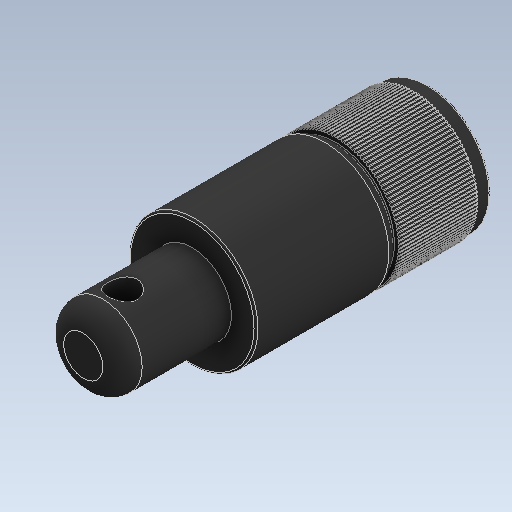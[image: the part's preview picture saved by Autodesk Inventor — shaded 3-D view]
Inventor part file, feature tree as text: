
AUTODESK INVENTOR PART (.ipt)
format: ipt  version: 2021 (Build 250183000, 183)  size: 415,744 bytes
history: native  units: mm
features: extrude x6, sketch x6, fillet x3, plane x1, pattern_circular x1
ambient origin geometry x8: Origin, YZ Plane, XZ Plane, XY Plane, X Axis, Y Axis, Z Axis, Center Point
bodies: Solid1 (feature_tree)
feature tree (17):
  extrude  "Extrusion1"  Depth=24.1mm TaperAngle=0.0deg
  extrude  "Extrusion2"  Depth=1.5mm TaperAngle=0.0deg
  plane  "Work Plane1"
  extrude  "Extrusion3"  Depth=0.2mm
  fillet  "Fillet1"  Radius=0.2mm
  extrude  "Extrusion4"  Depth=1.0mm
  pattern_circular  "Circular Pattern1"  Count=120 Angle=360.0deg
  extrude  "Extrusion5"  Depth=11.1mm TaperAngle=0.0deg
  extrude  "Extrusion6"  Depth=0.2mm
  fillet  "Fillet2"  Radius=31.2mm
  fillet  "Fillet3"  [1 undecoded]
  sketch  "Sketch1"  dims[d0=13.0mm d1=24.1mm d2=0.0mm]
  sketch  "Sketch2"  dims[d3=12.7mm d4=1.5mm d5=0.0mm]
  sketch  "Sketch4"  dims[d6=-9.5mm d7=0.5mm d8=0.2mm d9=0.0mm]
  sketch  "Sketch5"  dims[d10=1.0mm d11=0.25mm]
  sketch  "Sketch6"  dims[d12=0.0mm d13=0.0mm d14=1200.0mm d15=360.0deg]
  sketch  "Sketch7"  dims[d18=8.0mm d19=11.1mm d20=0.0mm d21=3.0mm d22=31.2mm d23=0.0mm d24=0.0mm d25=2.0mm d26=0.2mm]
note: 1 required parameter value undecoded (feature->parameter linkage not recoverable at this tier; creation-order binding heuristic only, values carry confidence <= 0.55)
